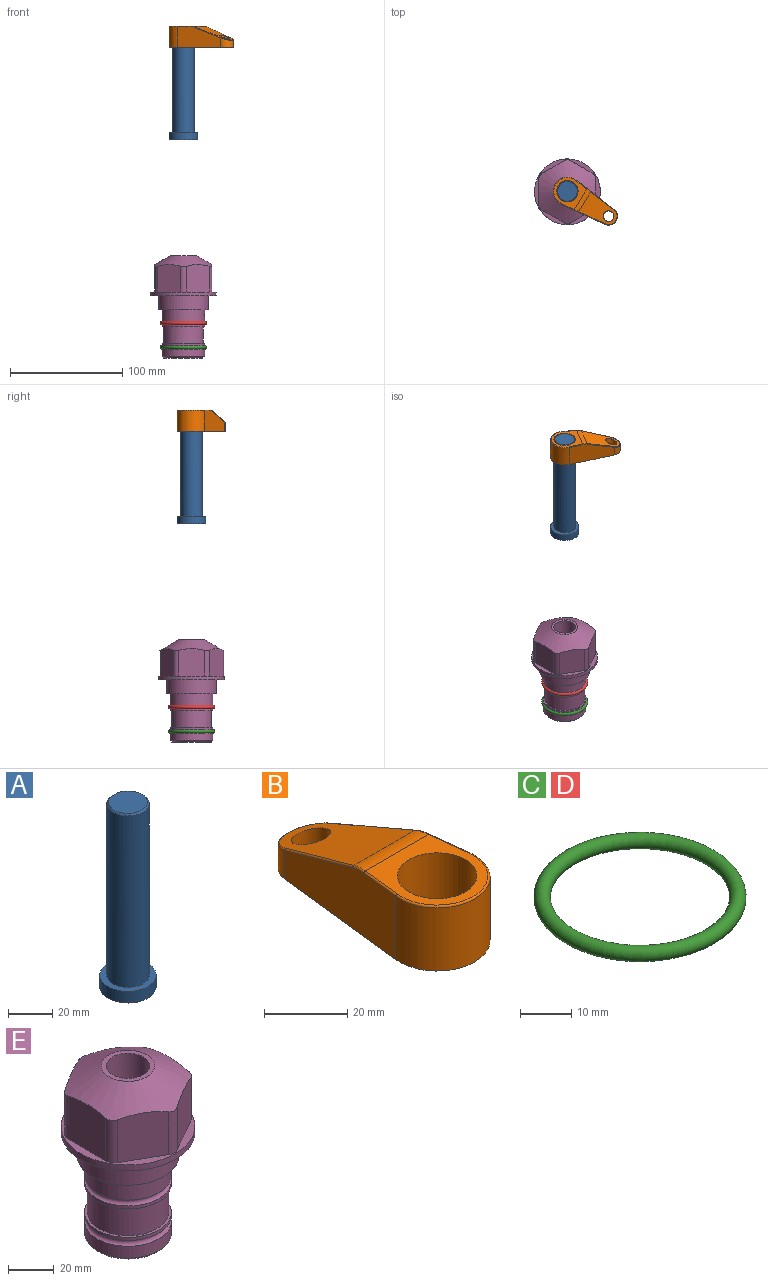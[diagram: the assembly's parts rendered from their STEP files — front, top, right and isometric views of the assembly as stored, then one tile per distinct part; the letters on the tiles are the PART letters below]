
ASSEMBLY  parts=5 mates=3
PART A: 6 faces, bbox 25.4x25.4x101.6 mm
  f0: plane 17.46x17.46mm, normal (0,0,1), area 239.5mm2, adj f5
  f1: plane 25.4x25.4mm, normal (0,0,-1), area 506.7mm2, adj f2
  f2: cylinder r=12.7mm len=25.4mm, axis (0,0,1), area 506.7mm2, adj f1,f3
  f3: plane 25.4x25.4mm, normal (0,0,1), area 221.7mm2, adj f2,f4
  f4: cylinder r=9.53mm len=94.46mm, axis (0,0,1), area 5653mm2, adj f3,f5
  f5: cone r=8.73mm half-angle=45deg, axis (0,0,-1), area 64.4mm2, adj f0,f4
PART B: 44 faces, bbox 27.5x64.5x19.1 mm
  f0: plane 2.3x0.95mm, normal (0,0,-1), area 1mm2, adj f25,f30,f34
  f1: plane 63.5x25.4mm, normal (0,0,-1), area 561.7mm2, adj f2,f3,f4,f5,f6,f7,f19,f20
  f2: cylinder r=12.7mm len=25.4mm, axis (0,0,-1), area 792.2mm2, adj f1,f3,f5,f13
  f3: plane 42.33x18.54mm, normal (0.99,0.11,0), area 647mm2, adj f1,f2,f4,f11,f12,f14
  f4: cylinder r=7.94mm len=15.78mm, axis (0,0,-1), area 158.6mm2, adj f1,f3,f5,f16
  f5: plane 42.33x18.54mm, normal (-0.99,0.11,0), area 647mm2, adj f1,f2,f4,f15,f17,f18
  f6: cylinder r=9.53mm len=19.05mm, axis (0,0,-1), area 1140.1mm2, adj f1,f8
  f7: cylinder r=4.76mm len=10.98mm, axis (0,0,-1), area 276.1mm2, adj f1,f9
  f8: plane 25.83x24.38mm, normal (0,0,1), area 262.2mm2, adj f6,f10,f11,f13,f15
  f9: plane 32.49x20.55mm, normal (0,0.34,0.94), area 489.9mm2, adj f7,f10,f14,f16,f18
  f10: cylinder r=12.7mm len=21.49mm, axis (-1,0,0), area 93.2mm2, adj f8,f9,f12,f17
  f11: cylinder r=0.51mm len=12.34mm, axis (0.11,-0.99,0), area 9.9mm2, adj f3,f8,f12,f13
  f12: bspline ~7.62x1.64mm, area 3.5mm2, adj f3,f10,f11,f14
  f13: torus R=12.19mm, axis (0,0,1), area 33.6mm2, adj f2,f8,f11,f15
  f14: cylinder r=0.51mm len=26.01mm, axis (0.1,-0.93,0.34), area 21.6mm2, adj f3,f9,f12,f16
  f15: cylinder r=0.51mm len=12.34mm, axis (0.11,0.99,0), area 9.9mm2, adj f5,f8,f13,f17
  f16: bspline ~15.78x7.05mm, area 15.7mm2, adj f4,f9,f14,f18
  f17: bspline ~7.62x1.64mm, area 3.5mm2, adj f5,f10,f15,f18
  f18: cylinder r=0.51mm len=26.01mm, axis (0.1,0.93,-0.34), area 21.6mm2, adj f5,f9,f16,f17
  f19: plane 21.6x14.29mm, normal (-0.99,-0.11,0), area 242.6mm2, adj f1,f26,f28,f34,f36,f38
  f20: plane 21.6x14.29mm, normal (0.99,-0.11,0), area 242.6mm2, adj f1,f27,f29,f37,f39,f41
  f21: cylinder r=12.7mm len=14.29mm, axis (0,0,-1), area 173.2mm2, adj f1,f26,f27,f30,f31,f33
  f22: cylinder r=7.94mm len=7.63mm, axis (0,0,-1), area 53.8mm2, adj f1,f28,f29,f42
  f23: plane 2.3x0.95mm, normal (0,0,-1), area 1mm2, adj f25,f33,f37
  f24: plane 17.94x12.32mm, normal (0,-0.34,-0.94), area 191.2mm2, adj f25,f38,f41,f42
  f25: cylinder r=9.53mm len=12.93mm, axis (-1,0,0), area 37.5mm2, adj f0,f23,f24,f31,f36,f39
  f26: cylinder r=1.59mm len=14.29mm, axis (0,0,-1), area 49mm2, adj f1,f19,f21,f32
  f27: cylinder r=1.59mm len=14.29mm, axis (0,0,-1), area 49mm2, adj f1,f20,f21,f35
  f28: cylinder r=1.59mm len=7.28mm, axis (0,0,-1), area 22.1mm2, adj f1,f19,f22,f40
  f29: cylinder r=1.59mm len=7.28mm, axis (0,0,-1), area 22.1mm2, adj f1,f20,f22,f43
  f30: torus R=14.29mm, axis (0,0,1), area 5.8mm2, adj f0,f21,f31,f32
  f31: bspline ~11.06x2.73mm, area 20.8mm2, adj f21,f25,f30,f33
  f32: sphere r=1.59mm, area 5.4mm2, adj f26,f30,f34
  f33: torus R=14.29mm, axis (0,0,1), area 5.8mm2, adj f21,f23,f31,f35
  f34: cylinder r=1.59mm len=1.68mm, axis (-0.11,0.99,0), area 2.4mm2, adj f0,f19,f32,f36
  f35: sphere r=1.59mm, area 5.4mm2, adj f27,f33,f37
  f36: bspline ~5.82x2.33mm, area 7.7mm2, adj f19,f25,f34,f38
  f37: cylinder r=1.59mm len=1.68mm, axis (0.11,0.99,0), area 2.4mm2, adj f20,f23,f35,f39
  f38: cylinder r=1.59mm len=18.33mm, axis (0.1,-0.93,0.34), area 46.7mm2, adj f19,f24,f36,f40
  f39: bspline ~5.82x2.33mm, area 7.7mm2, adj f20,f25,f37,f41
  f40: sphere r=1.59mm, area 3.6mm2, adj f28,f38,f42
  f41: cylinder r=1.59mm len=18.33mm, axis (0.1,0.93,-0.34), area 46.7mm2, adj f20,f24,f39,f43
  f42: bspline ~8.31x1.84mm, area 15.3mm2, adj f22,f24,f40,f43
  f43: sphere r=1.59mm, area 3.6mm2, adj f29,f41,f42
PART C: 1 faces, bbox 44.7x44.7x3.2 mm
  f0: torus R=19.05mm, axis (0,0,1), area 1193.9mm2
PART D: same geometry as C
PART E: 36 faces, bbox 58.7x58.7x91.2 mm
  f0: cylinder r=17.78mm len=35.56mm, axis (0,0,1), area 1670.8mm2, adj f23,f24,f31
  f1: cylinder r=19.05mm len=38.1mm, axis (0,0,1), area 1191.9mm2, adj f26,f27,f30
  f2: plane 58.66x58.66mm, normal (0,0,-1), area 1150.6mm2, adj f3,f28
  f3: cylinder r=29.33mm len=58.66mm, axis (0,0,-1), area 585.1mm2, adj f2,f4
  f4: plane 58.66x58.66mm, normal (0,0,1), area 475.9mm2, adj f3,f5,f6,f7,f8,f9,f10,f11
  f5: plane 24.5x20.32mm, normal (-0.5,0.87,0), area 562.8mm2, adj f4,f15,f16,f17
  f6: plane 24.5x20.32mm, normal (0.5,0.87,0), area 562.8mm2, adj f4,f14,f15,f17
  f7: plane 24.5x23.48mm, normal (1,0,0), area 562.8mm2, adj f4,f13,f14,f17
  f8: plane 24.5x20.32mm, normal (0.5,-0.87,0), area 562.8mm2, adj f4,f12,f13,f17
  f9: plane 24.5x20.32mm, normal (-0.5,-0.87,0), area 562.8mm2, adj f4,f11,f12,f17
  f10: plane 24.5x23.48mm, normal (-1,0,0), area 562.8mm2, adj f4,f11,f16,f17
  f11: cylinder r=5.08mm len=23.01mm, axis (0,0,-1), area 121.2mm2, adj f4,f9,f10,f17
  f12: cylinder r=5.08mm len=23.01mm, axis (0,0,-1), area 121.2mm2, adj f4,f8,f9,f17
  f13: cylinder r=5.08mm len=23.01mm, axis (0,0,-1), area 121.2mm2, adj f4,f7,f8,f17
  f14: cylinder r=5.08mm len=23.01mm, axis (0,0,-1), area 121.2mm2, adj f4,f6,f7,f17
  f15: cylinder r=5.08mm len=23.01mm, axis (0,0,-1), area 121.2mm2, adj f4,f5,f6,f17
  f16: cylinder r=5.08mm len=23.01mm, axis (0,0,-1), area 121.2mm2, adj f4,f5,f10,f17
  f17: cone r=11.73mm half-angle=60deg, axis (0,0,-1), area 2071.8mm2, adj f5,f6,f7,f8,f9,f10,f11,f12
  f18: plane 23.46x23.46mm, normal (0,0,1), area 147.4mm2, adj f17,f35
  f19: plane 34.93x34.93mm, normal (0,0,-1), area 958mm2, adj f29
  f20: cylinder r=19.05mm len=38.1mm, axis (0,0,1), area 760.1mm2, adj f21,f29
  f21: torus R=19.05mm, axis (0,0,1), area 565.3mm2, adj f20,f22
  f22: cylinder r=19.05mm len=38.1mm, axis (0,0,1), area 190mm2, adj f21,f23
  f23: plane 38.1x38.1mm, normal (0,0,1), area 146.9mm2, adj f0,f22
  f24: plane 38.1x38.1mm, normal (0,0,-1), area 146.9mm2, adj f0,f25
  f25: cylinder r=19.05mm len=38.1mm, axis (0,0,1), area 190mm2, adj f24,f26
  f26: torus R=19.05mm, axis (0,0,1), area 565.3mm2, adj f1,f25
  f27: plane 44.45x44.45mm, normal (0,0,-1), area 411.7mm2, adj f1,f28
  f28: cylinder r=22.23mm len=44.45mm, axis (0,0,1), area 1773.5mm2, adj f2,f27
  f29: cone r=19.05mm half-angle=45deg, axis (0,0,1), area 257.5mm2, adj f19,f20
  f30: cylinder r=3.17mm len=6.75mm, axis (-1,0,0), area 128mm2, adj f1,f33
  f31: cylinder r=3.17mm len=6.35mm, axis (-1,0,0), area 102.5mm2, adj f0,f33
  f32: plane 25.4x25.4mm, normal (0,0,1), area 506.7mm2, adj f33
  f33: cylinder r=12.7mm len=66.42mm, axis (0,0,-1), area 5236.2mm2, adj f30,f31,f32,f34
  f34: cone r=9.53mm half-angle=30deg, axis (0,0,-1), area 443.4mm2, adj f33,f35
  f35: cylinder r=9.53mm len=19.05mm, axis (0,0,-1), area 849mm2, adj f18,f34
PLACE A rot(axis=(0,0,-1),31.1deg) t=(0,0,166.79)mm
PLACE B rot(axis=(0,0,-1),121.1deg) t=(0,0,221.4)mm
PLACE C t=(0,0,-21.59)mm
PLACE D at identity
PLACE E at identity fixed
MATE fastened C.f0 <-> E.f0  axis (0,0,1) through (0,0,-46.1)mm
MATE cylindrical A.f2 <-> E.f0  axis (0,0,1) through (0,0,192.43)mm
MATE fastened B.f2 <-> A.f2  axis (0,0,1) through (0,0,240.45)mm
